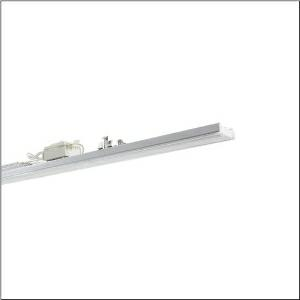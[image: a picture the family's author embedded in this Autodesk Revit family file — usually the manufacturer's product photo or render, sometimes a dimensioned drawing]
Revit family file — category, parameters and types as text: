
# Revit family: licross_r__21_recessed_ho_52tl12dn4axm_2663
name_source: partatom
category: Lighting Fixtures
units: mm (PartAtom-declared; Revit-internal decimal feet)

## family parameters
Cut with Voids When Loaded = No
Host = Face
Light Source = No
Part Type = Normal
Room Calculation Point = No
Round Connector Dimension = Use Diameter
Shared = No

## types (1)
- --- (1 x LED, 10000 lm, 54.6 W, 4000K)
    Apparent Load = 55 VA
    CIE Flux Codes = 69 91 98 100 100
    Color Rendering = 80
    Color Temperature = 4000K
    Default Elevation = 1800 mm
    Description = Licross® 21 Recessed HO, luminaire insert, of sheet steel, galvanised, coil coated, white, length: 1.500mm, width: 66mm, height: 67mm, LED rated luminous flux: 10.000lm, light colour: 840, control gear: DALI 2, with plug, 5-pole, with phase selection, mains connection: 220..240V, AC, 50/60Hz, rated input power: 55W, halogen-free wiring, primary optical cover: cover, of PMMA, light emission: direct distribution, primary light characteristic: symmetric, protection rating (complete): IP40, insulation class (complete): insulation class I (protective earthing), certification: CE, ENEC, VDE, UKCA, protection symbol: D if used in an environment without relevant dust loads with corresponding accessories, impact resistance: IK06, permissible ambient temperature for indoor applications: -25..+40°C, corresponds to IFS (International Featured Standards) requirements for safety and quality in the food industry, reducing of maximum allowable ambient temperature of 5°C with ceiling mounting, LABS conformity tested according to VDMA 24364:2018-05, packaging unit: 1 piece
    Height = 58 mm
    Lamp = 1 x LED
    Lamp Light Flux = 10000 lm
    Lamp Power = 54.6 W
    Lamp count = 1
    Length = 1500 mm
    Luminous efficacy = 183 lm/W
    Manufacturer = Siteco
    ModVariant = No
    Model = 52TL12DN4AXM
    Mounting Place = Ceiling
    Mounting Type = Pendant
    Number of Poles = 1
    OnlyDefault = Yes
    Power Factor = 1
    Product Name = Licross® 21 Recessed HO
    Product group = luminaire insert
    ProductGroupID = 902
    Protection Class = Protection class I
    Protection Degree = IP 40
    RLX_Detail_Level = 1
    RLX_Emergency_Light_Flux = 0 lm
    RLX_Emergency_Type = 0
    RLX_Emergency_Type_DB = No
    RlxData = <blob elided: 24373 chars, md5=6e6e92ca>
    Socket = socket
    Standby Power = 0 W
    System Light Flux = 10000 lm
    System Power = 55 W
    Type Comments = factory setting: luminous flux: 100 % | dim-lin: 254 | 313 mA
    Type Image = l_1296930.jpg
    URL = http://relux.com
    VarID = @adj_116518
    Voltage = 0 V
    Weight = 0.00 kg
    Width = 66 mm

## geometry (parser evidence)
native form markers: Blend x4, Sweep x9
no freeform markers — native parametric forms only
